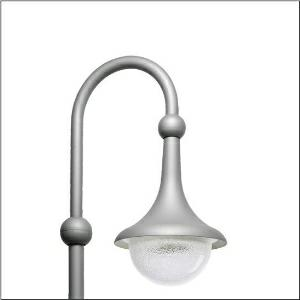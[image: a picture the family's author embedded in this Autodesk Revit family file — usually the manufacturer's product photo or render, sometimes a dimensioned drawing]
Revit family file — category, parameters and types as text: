
# Revit family: kleine_glocke___st1_2a_5xa1573k1b208_586f
name_source: partatom
category: Lighting Fixtures
units: mm (PartAtom-declared; Revit-internal decimal feet)

## family parameters
Cut with Voids When Loaded = No
Host = Face
Light Source = No
Part Type = Normal
Room Calculation Point = No
Round Connector Dimension = Use Diameter
Shared = No

## types (1)
- --- (1 x LED, 1750 lm, 13.2 W, 4000K)
    Apparent Load = 13 VA
    CIE Flux Codes = 28 64 93 98 100
    Color Rendering = 70
    Color Temperature = 4000K
    Default Elevation = 1800 mm
    Description = Small Bell, mast luminaire, primary light control with 3 zone facetted reflector, of plastic, aluminium vaporised, primary optical cover: enclosure, of PMMA, transparent structured, light distribution: ST1.2a, light emission: direct distribution, primary light characteristic: asymmetric, installation type: suspended mounting, LED, High Power LED, rated luminous flux: 1.750lm, luminous efficacy: 133lm/W, light colour: 740, colour temperature: 4000K, control gear: Plus, control: flexible luminous flux parameterisation, time-dependent luminous flux control, constant luminous flux control, digital communication interface, power reduction, electronic power reduction, mains connection: 230..240V, AC, 50/60Hz, start of lifetime: 13W, end of service life: 14W, reduction: 7W, luminaire housing, bell-shaped, of glass-fibre reinforced polyester, coated, Siteco® metallic grey (DB 702S), please order curved mast extension separately, diameter: 430mm, height: 575mm, mounting height: 2.5..4.0m, protection rating (complete): IP54, insulation class (complete): insulation class II (safety insulation), certification: CE, ENEC, VDE, impact resistance: IK07, standard-compliant lighting for roads and squares, packaging unit: 1 piece

Light Distribution: ST1.2a
    Height = 575 mm
    Lamp = 1 x LED
    Lamp Light Flux = 1750 lm
    Lamp Power = 13.2 W
    Lamp count = 1
    Length = 430 mm
    Luminous efficacy = 133 lm/W
    Manufacturer = Siteco
    ModVariant = No
    Model = 5XA1573K1B208
    Number of Poles = 1
    OnlyDefault = Yes
    Power Factor = 1
    Product Name = Kleine Glocke | ST1.2a
    Product group = mast luminaire | pylon annexe
    ProductGroupID = 6201
    Protection Class = Protection class II
    Protection Degree = IP 54
    RLX_Detail_Level = 1
    RLX_Emergency_Light_Flux = 0 lm
    RLX_Emergency_Type = 0
    RLX_Emergency_Type_DB = No
    RlxData = <blob elided: 52137 chars, md5=e68b117f>
    Socket = socket
    Standby Power = 0 W
    System Light Flux = 1750 lm
    System Power = 13 W
    Type Comments = factory setting: luminous flux: 100 % | dim-lin: 254 | 249 mA
    Type Image = l_1347695.jpg
    URL = http://relux.com
    VarID = @adj_197864
    Voltage = 0 V
    Weight = 0.00 kg
    Width = 0 mm  [stored 0 ft]

note: [stored X ft] marks values corroborated as IEEE doubles in the binary element streams (Revit-internal decimal feet)

## geometry (parser evidence)
native form markers: Blend x4, Sweep x10
no freeform markers — native parametric forms only
